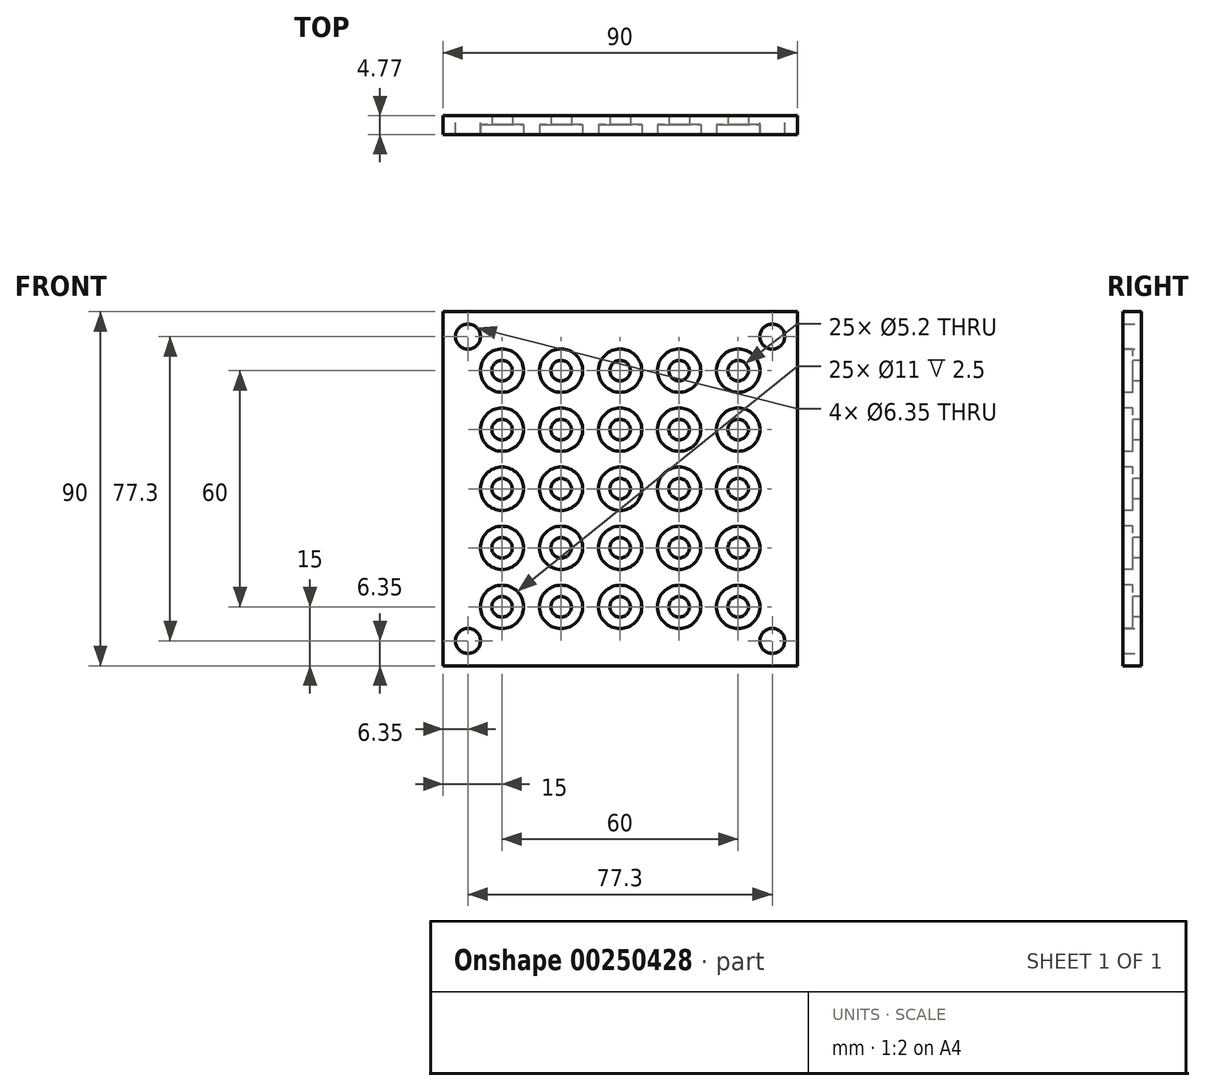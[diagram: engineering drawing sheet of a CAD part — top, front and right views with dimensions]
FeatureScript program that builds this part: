
annotation { "Feature Type Name" : "Feature", "Feature Type Description" : "" }
export const myFeature = defineFeature(function(context is Context, id is Id, definition is map)
    precondition{}
    {
        {
            var Q0;
            Q0=qCreatedBy(makeId("Front.planeOp"),FACE);
            var sketch = newSketch(context, id + "F0", { "sketchPlane" : qUnion([Q0])});
            skLineSegment(sketch, "E0.bottom", {"start": v(-45, 45) * mm, "end": v(45, 45) * mm});
            skLineSegment(sketch, "E0.top", {"start": v(-45, -45) * mm, "end": v(45, -45) * mm});
            skLineSegment(sketch, "E0.left", {"start": v(-45, 45) * mm, "end": v(-45, -45) * mm});
            skLineSegment(sketch, "E0.right", {"start": v(45, 45) * mm, "end": v(45, -45) * mm});
            skCircle(sketch, "E1", {"center": v(-38.65, 38.65) * mm, "radius": 3.18 * mm});
            skCircle(sketch, "E2", {"center": v(38.65, 38.65) * mm, "radius": 3.18 * mm});
            skCircle(sketch, "E3", {"center": v(38.65, -38.65) * mm, "radius": 3.18 * mm});
            skCircle(sketch, "E4", {"center": v(-38.65, -38.65) * mm, "radius": 3.18 * mm});
            skLineSegment(sketch, "E5.bottom", {"start": v(-50, 50) * mm, "end": v(50, 50) * mm, "construction": true});
            skLineSegment(sketch, "E5.top", {"start": v(-50, -50) * mm, "end": v(50, -50) * mm, "construction": true});
            skLineSegment(sketch, "E5.left", {"start": v(-50, 50) * mm, "end": v(-50, -50) * mm, "construction": true});
            skLineSegment(sketch, "E5.right", {"start": v(50, 50) * mm, "end": v(50, -50) * mm, "construction": true});
            skSolve(sketch);
        }
        {
            var Q0;
            Q0 = qSketchRegion(id + "F0", true);
            extrude(context, id + "F1", {"entities" : qUnion([Q0]), "depth" : 4.77 * mm});
        }
        {
            var Q0;
            Q0=makeQuery(id+"F1.opExtrude","CAP_FACE",FACE,{"disambiguationData":[OSD([sQuery(id+"F0.wireOp",EDGE,"E0.bottom"),sQuery(id+"F0.wireOp",EDGE,"E0.top"),sQuery(id+"F0.wireOp",EDGE,"E0.left"),sQuery(id+"F0.wireOp",EDGE,"E0.right"),sQuery(id+"F0.wireOp",EDGE,"E1"),sQuery(id+"F0.wireOp",EDGE,"E2"),sQuery(id+"F0.wireOp",EDGE,"E3"),sQuery(id+"F0.wireOp",EDGE,"E4")])],"isStart":false});
            var sketch = newSketch(context, id + "F2", { "sketchPlane" : qUnion([Q0])});
            skCircle(sketch, "E6", {"center": v(-30, 30) * mm, "radius": 2.6 * mm});
            skCircle(sketch, "E7.0.1.0", {"center": v(-30, 15) * mm, "radius": 2.6 * mm});
            skCircle(sketch, "E7.0.2.0", {"center": v(-30, 0) * mm, "radius": 2.6 * mm});
            skCircle(sketch, "E7.0.3.0", {"center": v(-30, -15) * mm, "radius": 2.6 * mm});
            skCircle(sketch, "E7.0.4.0", {"center": v(-30, -30) * mm, "radius": 2.6 * mm});
            skCircle(sketch, "E7.1.0.0", {"center": v(-15, 30) * mm, "radius": 2.6 * mm});
            skCircle(sketch, "E7.1.1.0", {"center": v(-15, 15) * mm, "radius": 2.6 * mm});
            skCircle(sketch, "E7.1.2.0", {"center": v(-15, 0) * mm, "radius": 2.6 * mm});
            skCircle(sketch, "E7.1.3.0", {"center": v(-15, -15) * mm, "radius": 2.6 * mm});
            skCircle(sketch, "E7.1.4.0", {"center": v(-15, -30) * mm, "radius": 2.6 * mm});
            skCircle(sketch, "E7.2.0.0", {"center": v(0, 30) * mm, "radius": 2.6 * mm});
            skCircle(sketch, "E7.2.1.0", {"center": v(0, 15) * mm, "radius": 2.6 * mm});
            skCircle(sketch, "E7.2.2.0", {"center": v(0, 0) * mm, "radius": 2.6 * mm});
            skCircle(sketch, "E7.2.3.0", {"center": v(0, -15) * mm, "radius": 2.6 * mm});
            skCircle(sketch, "E7.2.4.0", {"center": v(0, -30) * mm, "radius": 2.6 * mm});
            skCircle(sketch, "E7.3.0.0", {"center": v(15, 30) * mm, "radius": 2.6 * mm});
            skCircle(sketch, "E7.3.1.0", {"center": v(15, 15) * mm, "radius": 2.6 * mm});
            skCircle(sketch, "E7.3.2.0", {"center": v(15, 0) * mm, "radius": 2.6 * mm});
            skCircle(sketch, "E7.3.3.0", {"center": v(15, -15) * mm, "radius": 2.6 * mm});
            skCircle(sketch, "E7.3.4.0", {"center": v(15, -30) * mm, "radius": 2.6 * mm});
            skCircle(sketch, "E7.4.0.0", {"center": v(30, 30) * mm, "radius": 2.6 * mm});
            skCircle(sketch, "E7.4.1.0", {"center": v(30, 15) * mm, "radius": 2.6 * mm});
            skCircle(sketch, "E7.4.2.0", {"center": v(30, 0) * mm, "radius": 2.6 * mm});
            skCircle(sketch, "E7.4.3.0", {"center": v(30, -15) * mm, "radius": 2.6 * mm});
            skCircle(sketch, "E7.4.4.0", {"center": v(30, -30) * mm, "radius": 2.6 * mm});
            skLineSegment(sketch, "E7.direction1", {"start": v(-30, 30) * mm, "end": v(-15, 30) * mm, "construction": true});
            skLineSegment(sketch, "E7.direction2", {"start": v(-30, 30) * mm, "end": v(-30, 15) * mm, "construction": true});
            skSolve(sketch);
        }
        {
            var Q0;
            Q0 = qSketchRegion(id + "F2", true);
            extrude(context, id + "F3", {"entities" : qUnion([Q0]), "operationType" : NewBodyOperationType.REMOVE, "endBound" : BoundingType.UP_TO_NEXT, "oppositeDirection" : true, "depth" : 25 * mm});
        }
        {
            var Q0;
            Q0=makeQuery(id+"F1.opExtrude","CAP_FACE",FACE,{"disambiguationData":[OSD([sQuery(id+"F0.wireOp",EDGE,"E0.bottom"),sQuery(id+"F0.wireOp",EDGE,"E0.top"),sQuery(id+"F0.wireOp",EDGE,"E0.left"),sQuery(id+"F0.wireOp",EDGE,"E0.right"),sQuery(id+"F0.wireOp",EDGE,"E1"),sQuery(id+"F0.wireOp",EDGE,"E2"),sQuery(id+"F0.wireOp",EDGE,"E3"),sQuery(id+"F0.wireOp",EDGE,"E4")])],"isStart":false});
            var sketch = newSketch(context, id + "F4", { "sketchPlane" : qUnion([Q0])});
            skCircle(sketch, "E8", {"center": v(-30, 30) * mm, "radius": 5.5 * mm});
            skCircle(sketch, "E9.0.1.0", {"center": v(-30, 15) * mm, "radius": 5.5 * mm});
            skCircle(sketch, "E9.0.2.0", {"center": v(-30, 0) * mm, "radius": 5.5 * mm});
            skCircle(sketch, "E9.0.3.0", {"center": v(-30, -15) * mm, "radius": 5.5 * mm});
            skCircle(sketch, "E9.0.4.0", {"center": v(-30, -30) * mm, "radius": 5.5 * mm});
            skCircle(sketch, "E9.1.0.0", {"center": v(-15, 30) * mm, "radius": 5.5 * mm});
            skCircle(sketch, "E9.1.1.0", {"center": v(-15, 15) * mm, "radius": 5.5 * mm});
            skCircle(sketch, "E9.1.2.0", {"center": v(-15, 0) * mm, "radius": 5.5 * mm});
            skCircle(sketch, "E9.1.3.0", {"center": v(-15, -15) * mm, "radius": 5.5 * mm});
            skCircle(sketch, "E9.1.4.0", {"center": v(-15, -30) * mm, "radius": 5.5 * mm});
            skCircle(sketch, "E9.2.0.0", {"center": v(0, 30) * mm, "radius": 5.5 * mm});
            skCircle(sketch, "E9.2.1.0", {"center": v(0, 15) * mm, "radius": 5.5 * mm});
            skCircle(sketch, "E9.2.2.0", {"center": v(0, 0) * mm, "radius": 5.5 * mm});
            skCircle(sketch, "E9.2.3.0", {"center": v(0, -15) * mm, "radius": 5.5 * mm});
            skCircle(sketch, "E9.2.4.0", {"center": v(0, -30) * mm, "radius": 5.5 * mm});
            skCircle(sketch, "E9.3.0.0", {"center": v(15, 30) * mm, "radius": 5.5 * mm});
            skCircle(sketch, "E9.3.1.0", {"center": v(15, 15) * mm, "radius": 5.5 * mm});
            skCircle(sketch, "E9.3.2.0", {"center": v(15, 0) * mm, "radius": 5.5 * mm});
            skCircle(sketch, "E9.3.3.0", {"center": v(15, -15) * mm, "radius": 5.5 * mm});
            skCircle(sketch, "E9.3.4.0", {"center": v(15, -30) * mm, "radius": 5.5 * mm});
            skCircle(sketch, "E9.4.0.0", {"center": v(30, 30) * mm, "radius": 5.5 * mm});
            skCircle(sketch, "E9.4.1.0", {"center": v(30, 15) * mm, "radius": 5.5 * mm});
            skCircle(sketch, "E9.4.2.0", {"center": v(30, 0) * mm, "radius": 5.5 * mm});
            skCircle(sketch, "E9.4.3.0", {"center": v(30, -15) * mm, "radius": 5.5 * mm});
            skCircle(sketch, "E9.4.4.0", {"center": v(30, -30) * mm, "radius": 5.5 * mm});
            skLineSegment(sketch, "E9.direction1", {"start": v(-30, 30) * mm, "end": v(-15, 30) * mm, "construction": true});
            skLineSegment(sketch, "E9.direction2", {"start": v(-30, 30) * mm, "end": v(-30, 15) * mm, "construction": true});
            skSolve(sketch);
        }
        {
            var Q0;
            Q0 = qSketchRegion(id + "F4", true);
            extrude(context, id + "F5", {"entities" : qUnion([Q0]), "operationType" : NewBodyOperationType.REMOVE, "oppositeDirection" : true, "depth" : 2.5 * mm});
        }
    });
